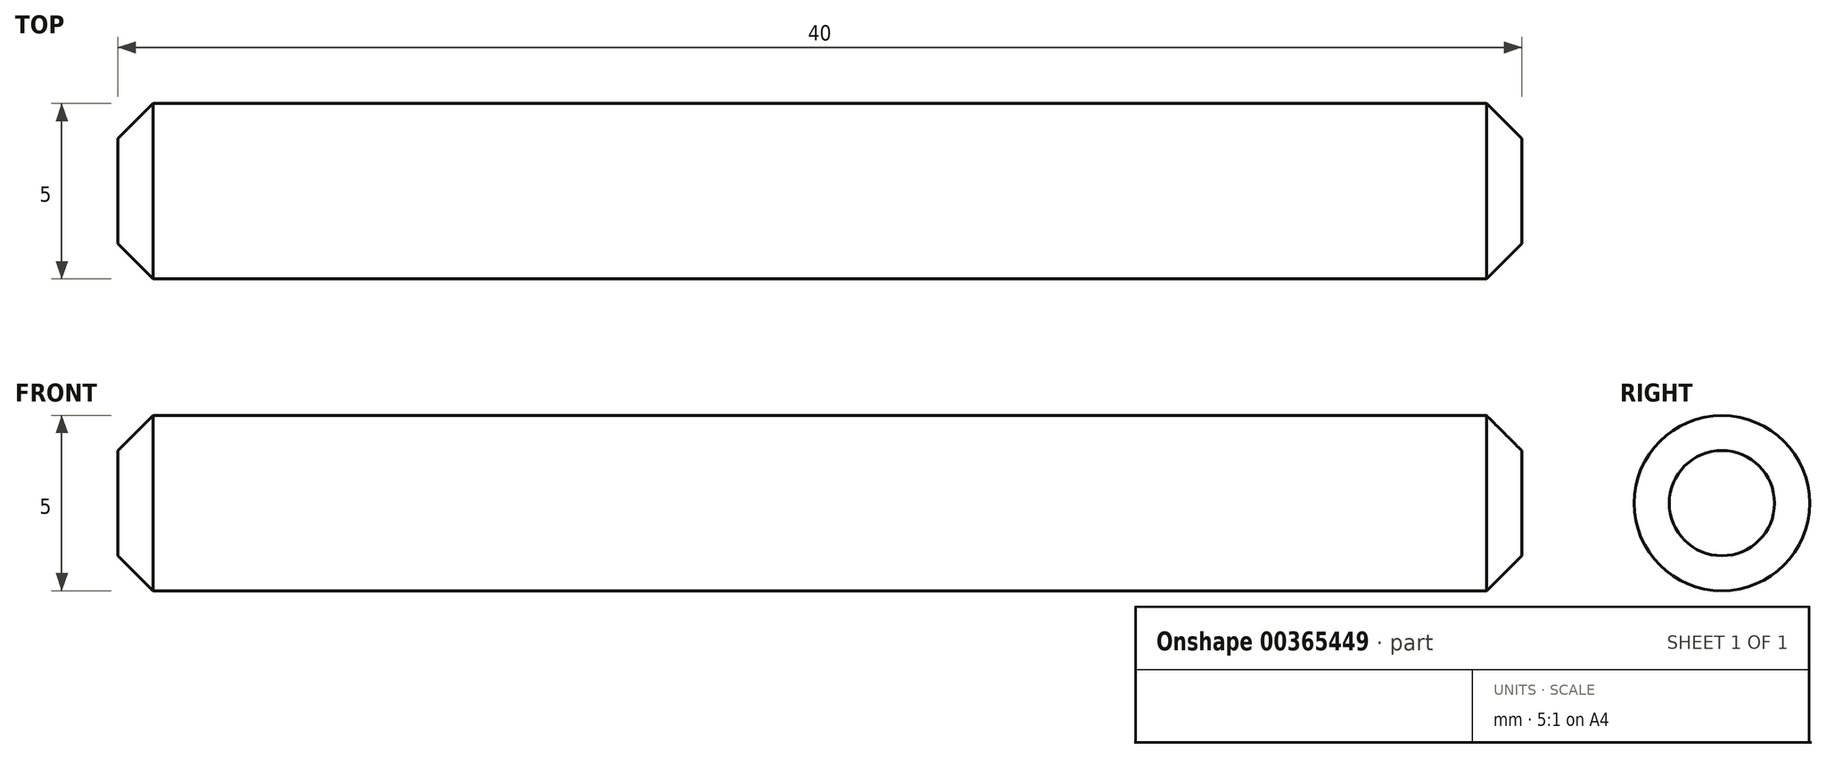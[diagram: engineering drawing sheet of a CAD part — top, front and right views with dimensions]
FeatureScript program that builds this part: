
annotation { "Feature Type Name" : "Feature", "Feature Type Description" : "" }
export const myFeature = defineFeature(function(context is Context, id is Id, definition is map)
    precondition{}
    {
        {
            var Q0;
            Q0=qCreatedBy(makeId("Front.planeOp"),FACE);
            var sketch = newSketch(context, id + "F0", { "sketchPlane" : qUnion([Q0])});
            skLineSegment(sketch, "E0", {"start": v(2.2, 0) * mm, "end": v(2.2, 2.5) * mm});
            skLineSegment(sketch, "E1", {"start": v(2.2, 2.5) * mm, "end": v(-37.8, 2.5) * mm});
            skLineSegment(sketch, "E2", {"start": v(-37.8, 2.5) * mm, "end": v(-37.8, 0) * mm});
            skLineSegment(sketch, "E3", {"start": v(-37.8, 0) * mm, "end": v(2.2, 0) * mm});
            skSolve(sketch);
        }
        {
            var Q0;
            Q0=makeQuery(id+"F0.imprint","IMPRINT",FACE,{"disambiguationData":[TD([[makeQuery(id+"F0.imprint","IMPRINT",EDGE,{"derivedFrom":sQuery(id+"F0.wireOp",EDGE,"E0")}),1.0]])]});
            var Q1;
            Q1=sQuery(id+"F0.wireOp",EDGE,"E3");
            revolve(context, id + "F1", {"entities" : qUnion([Q0]), "axis" : qUnion([Q1]), "revolveType" : RevolveType.FULL});
        }
        {
            var Q0;
            Q0=makeQuery(id+"F1.opRevolve","SWEPT_EDGE",EDGE,{"disambiguationData":[OSD([sQuery(id+"F0.wireOp",EDGE,"E1"),sQuery(id+"F0.wireOp",EDGE,"E2")])]});
            var Q1;
            Q1=makeQuery(id+"F1.opRevolve","SWEPT_EDGE",EDGE,{"disambiguationData":[OSD([sQuery(id+"F0.wireOp",EDGE,"E0"),sQuery(id+"F0.wireOp",EDGE,"E1")])]});
            chamfer(context, id + "F2", {"entities" : qUnion([Q0, Q1]), "width" : 1 * mm, "tangentPropagation" : true});
        }
    });
